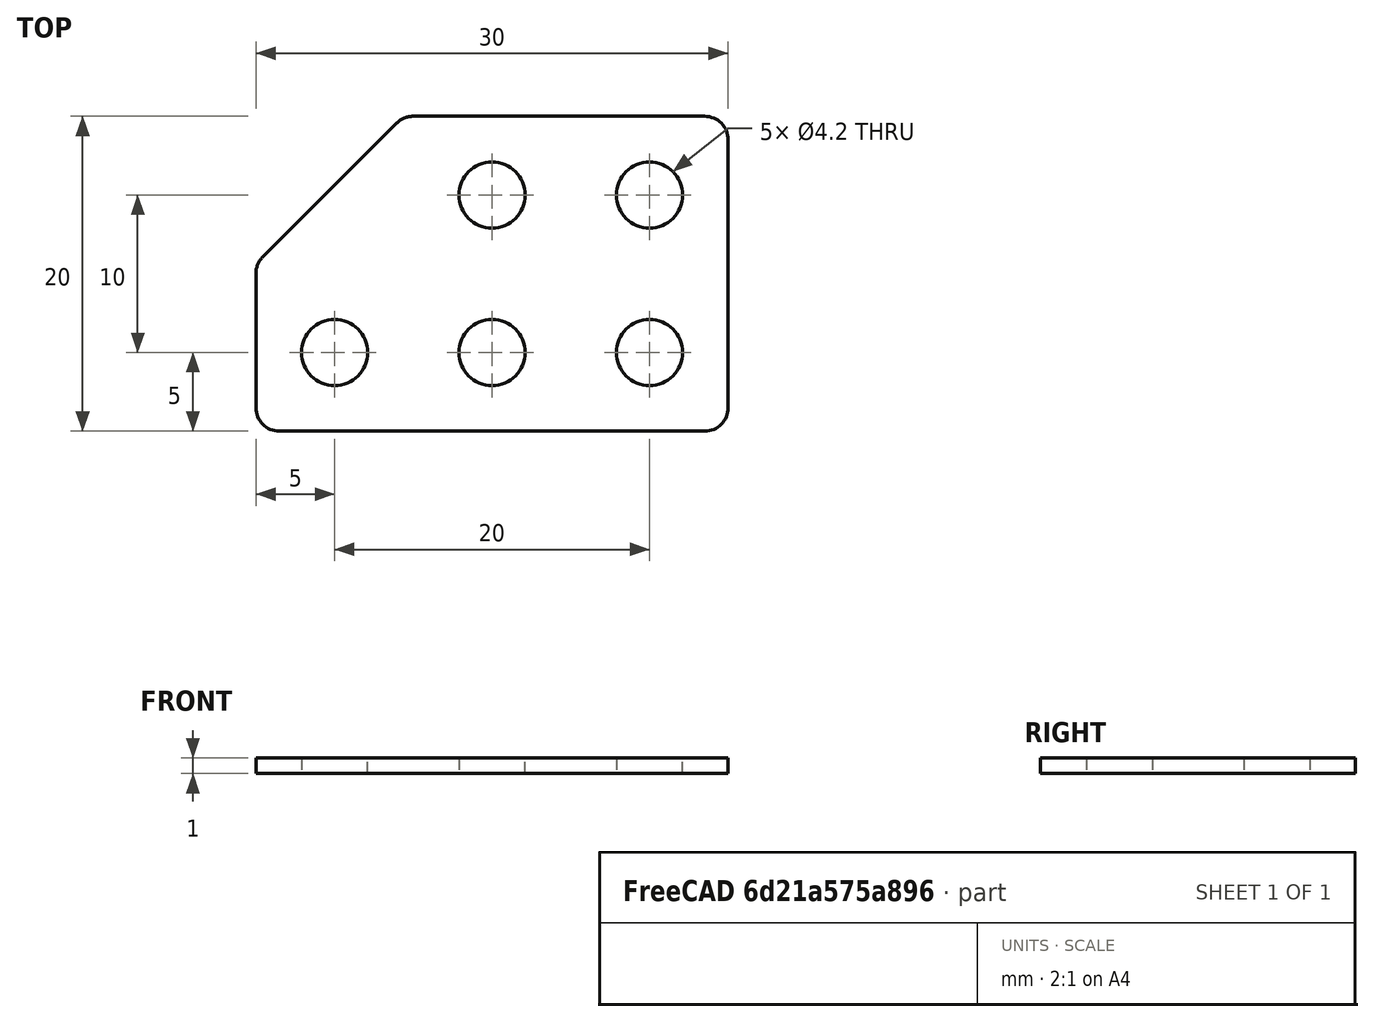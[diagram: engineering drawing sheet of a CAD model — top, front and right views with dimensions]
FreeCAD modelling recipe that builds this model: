
FCSTD DOCUMENT  (FreeCAD 0.16RUnknown)
Label: strip_2x3_corner
License: All rights reserved
LicenseURL: http://en.wikipedia.org/wiki/All_rights_reserved
objects: Sketcher::SketchObject×1, PartDesign::Pad×1
note: 3 computed .brp shape members not serialized (recipe doc carries the construction recipe); baked Part::Feature solids carry a one-line shape summary decoded from their .brp

FEATURE [Sketcher::SketchObject] Sketch
  sketch-geometry (18):
    g0: LineSegment StartX=5 StartY=15 StartZ=0 EndX=23.5 EndY=15 EndZ=0
    g1: LineSegment StartX=25 StartY=13.5 StartZ=0 EndX=25 EndY=-3.5 EndZ=0
    g2: LineSegment StartX=23.5 StartY=-5 StartZ=0 EndX=-3.5 EndY=-5 EndZ=0
    g3: LineSegment StartX=-5 StartY=-3.5 StartZ=0 EndX=-5 EndY=5 EndZ=0
    g4: ArcOfCircle CenterX=23.5 CenterY=13.5 CenterZ=0 NormalX=0 NormalY=0 NormalZ=1 Radius=1.5 StartAngle=0 EndAngle=1.5708
    g5: ArcOfCircle CenterX=23.5 CenterY=-3.5 CenterZ=0 NormalX=0 NormalY=0 NormalZ=1 Radius=1.5 StartAngle=4.71239 EndAngle=6.28319
    g6: ArcOfCircle CenterX=-3.5 CenterY=-3.5 CenterZ=0 NormalX=0 NormalY=0 NormalZ=1 Radius=1.5 StartAngle=3.14159 EndAngle=4.71239
    g7: Circle CenterX=0 CenterY=0 CenterZ=0 NormalX=0 NormalY=0 NormalZ=1 Radius=2.1
    g8: Circle CenterX=10 CenterY=0 CenterZ=0 NormalX=0 NormalY=0 NormalZ=1 Radius=2.1
    g9: LineSegment [constr] StartX=0 StartY=0 StartZ=0 EndX=10 EndY=0 EndZ=0
    g10: Circle CenterX=20 CenterY=0 CenterZ=0 NormalX=0 NormalY=0 NormalZ=1 Radius=2.1
    g11: LineSegment [constr] StartX=10 StartY=0 StartZ=0 EndX=20 EndY=0 EndZ=0
    g12: Circle CenterX=10 CenterY=10 CenterZ=0 NormalX=0 NormalY=0 NormalZ=1 Radius=2.1
    g13: Circle CenterX=20 CenterY=10 CenterZ=0 NormalX=0 NormalY=0 NormalZ=1 Radius=2.1
    g14: LineSegment [constr] StartX=10 StartY=10 StartZ=0 EndX=20 EndY=10 EndZ=0
    g15: LineSegment StartX=-4.56066 StartY=6.06066 StartZ=0 EndX=3.93934 EndY=14.5607 EndZ=0
    g16: ArcOfCircle CenterX=-3.5 CenterY=5 CenterZ=0 NormalX=0 NormalY=0 NormalZ=1 Radius=1.5 StartAngle=2.35619 EndAngle=3.14159
    g17: ArcOfCircle CenterX=5 CenterY=13.5 CenterZ=0 NormalX=0 NormalY=0 NormalZ=1 Radius=1.5 StartAngle=1.5708 EndAngle=2.35619
  constraints (45):
    c: Horizontal(g0)
    c: Horizontal(g2)
    c: Vertical(g1)
    c: Vertical(g3)
    c: Tangent(g0,g4) = 1.5708
    c: Tangent(g1,g4) = 1.5708
    c: Tangent(g1,g5) = 1.5708
    c: Tangent(g2,g5) = 1.5708
    c: Tangent(g3,g6) = 1.5708
    c: Tangent(g2,g6) = 1.5708
    c: Coincident(g7,g-1)
    c: Radius(g7) = 2.1
    c: Equal(g7,g8) = 2.1
    c: Coincident(g7,g9)
    c: Coincident(g8,g9)
    c: Distance(g9) = 10
    c: Angle(g9) = 0
    c: Equal(g7,g10) = 2.1
    c: Coincident(g8,g11)
    c: Coincident(g10,g11)
    c: Equal(g9,g11)
    c: Parallel(g11,g9)
    c: Coincident(g12,g14)
    c: Coincident(g13,g14)
    c: Equal(g7,g12)
    c: Equal(g7,g13)
    c: DistanceY(g2,g10) = 5
    c: DistanceX(g10,g1) = 5
    c: DistanceX(g12,g13) = 10
    c: DistanceY(g10,g13) = 10
    c: DistanceY(g8,g12) = 10
    c: DistanceX(g10,g13) = 0
    c: Tangent(g15,g16) = 1.5708
    c: Tangent(g3,g16) = 1.5708
    c: Tangent(g15,g17) = 1.5708
    c: Tangent(g0,g17) = 1.5708
    c: Radius(g17) = 1.5
    c: Radius(g16) = 1.5
    c: DistanceX(g3,g1) = 30
    c: DistanceY(g2,g0) = 20
    c: Radius(g4) = 1.5
    c: Equal(g4,g5)
    c: Equal(g4,g6)
    c: DistanceX(g0,g1) = 20
    c: DistanceY(g2,g3) = 10
FEATURE [PartDesign::Pad] Pad
  Length = 1
  Length2 = 100
  Sketch = -> Sketch
  Type = 0
